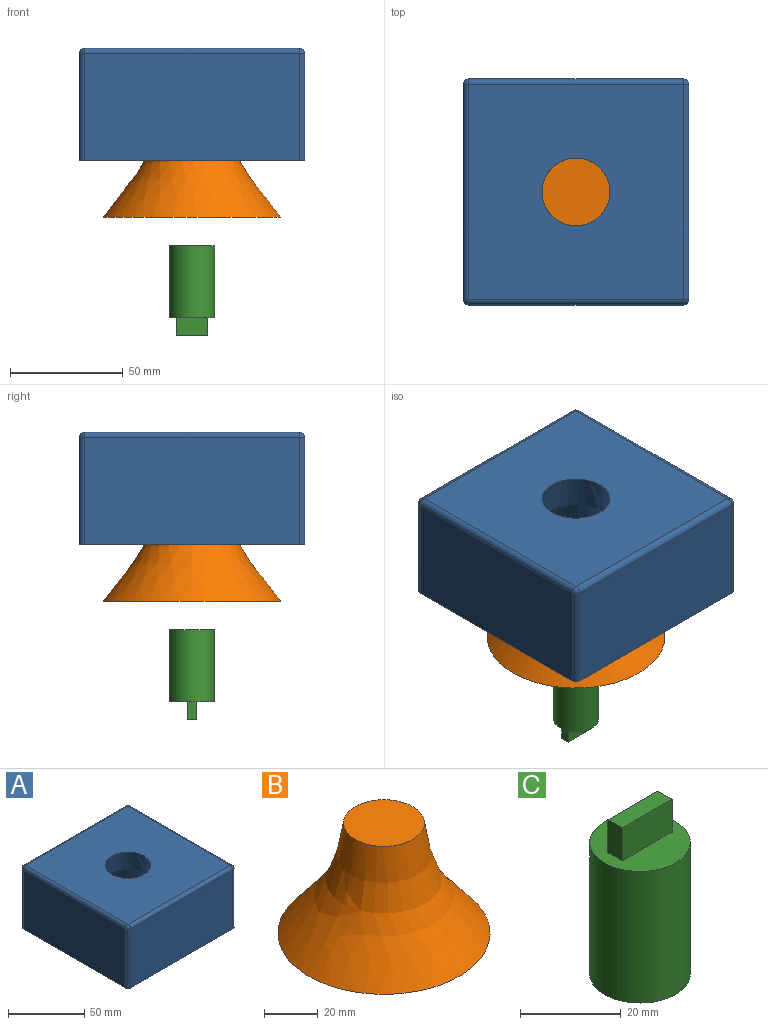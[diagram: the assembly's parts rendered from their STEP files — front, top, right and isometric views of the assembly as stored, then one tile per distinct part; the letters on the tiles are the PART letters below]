
ASSEMBLY  parts=3 mates=2
PART A: 19 faces, bbox 100x100x50 mm
  f0: plane 95x47.5mm, normal (0,-1,0), area 4512.5mm2, adj f5,f9,f15,f18
  f1: plane 95x47.5mm, normal (1,0,0), area 4512.5mm2, adj f5,f12,f16,f18
  f2: plane 95x47.5mm, normal (0,1,0), area 4512.5mm2, adj f5,f7,f11,f12
  f3: plane 95x47.5mm, normal (-1,0,0), area 4512.5mm2, adj f5,f7,f9,f10
  f4: plane 95x95mm, normal (0,0,1), area 8318.1mm2, adj f6,f10,f11,f15,f16
  f5: plane 100x100mm, normal (0,0,-1), area 5132.4mm2, adj f0,f1,f2,f3,f6,f7,f9,f12
  f6: revolved ~78.68x78.68mm, area 8666.1mm2, adj f4,f5
  f7: cylinder r=2.5mm len=47.5mm, axis (0,0,-1), area 186.5mm2, adj f2,f3,f5,f8
  f8: sphere r=2.5mm, area 9.8mm2, adj f7,f10,f11
  f9: cylinder r=2.5mm len=47.5mm, axis (0,0,1), area 186.5mm2, adj f0,f3,f5,f13
  f10: cylinder r=2.5mm len=95mm, axis (0,1,0), area 373.1mm2, adj f3,f4,f8,f13
  f11: cylinder r=2.5mm len=95mm, axis (1,0,0), area 373.1mm2, adj f2,f4,f8,f14
  f12: cylinder r=2.5mm len=47.5mm, axis (0,0,1), area 186.5mm2, adj f1,f2,f5,f14
  f13: sphere r=2.5mm, area 9.8mm2, adj f9,f10,f15
  f14: sphere r=2.5mm, area 9.8mm2, adj f11,f12,f16
  f15: cylinder r=2.5mm len=95mm, axis (-1,0,0), area 373.1mm2, adj f0,f4,f13,f17
  f16: cylinder r=2.5mm len=95mm, axis (0,-1,0), area 373.1mm2, adj f1,f4,f14,f17
  f17: sphere r=2.5mm, area 9.8mm2, adj f15,f16,f18
  f18: cylinder r=2.5mm len=47.5mm, axis (0,0,-1), area 186.5mm2, adj f0,f1,f5,f17
PART B: 5 faces, bbox 78.7x78.7x50 mm
  f0: plane 30x30mm, normal (0,0,1), area 706.9mm2, adj f1
  f1: revolved ~78.68x78.68mm, area 8666.1mm2, adj f0,f2
  f2: plane 78.68x78.68mm, normal (0,0,-1), area 4548mm2, adj f1,f3
  f3: cylinder r=10mm len=40mm, axis (0,0,-1), area 2513.3mm2, adj f2,f4
  f4: plane 20x20mm, normal (0,0,-1), area 314.2mm2, adj f3
PART C: 10 faces, bbox 20x20x40 mm
  f0: cylinder r=10mm len=32mm, axis (0,0,-1), area 2010.6mm2, adj f1,f2
  f1: plane 20x20mm, normal (0,0,1), area 258.2mm2, adj f0,f5,f6,f7,f8
  f2: plane 20x20mm, normal (0,0,-1), area 87.2mm2, adj f0,f3
  f3: cylinder r=8.5mm len=30.5mm, axis (0,0,-1), area 1628.9mm2, adj f2,f4
  f4: plane 17x17mm, normal (0,0,-1), area 227mm2, adj f3
  f5: plane 8x4mm, normal (-1,0,0), area 32mm2, adj f1,f6,f8,f9
  f6: plane 14x8mm, normal (0,-1,0), area 112mm2, adj f1,f5,f7,f9
  f7: plane 8x4mm, normal (1,0,0), area 32mm2, adj f1,f6,f8,f9
  f8: plane 14x8mm, normal (0,1,0), area 112mm2, adj f1,f5,f7,f9
  f9: plane 14x4mm, normal (0,0,1), area 56mm2, adj f5,f6,f7,f8
PLACE A t=(4.96,13.99,-1.33)mm
PLACE B t=(4.96,13.99,-26.24)mm fixed
PLACE C rot(axis=(1,0,0),180deg) t=(4.96,13.99,-38.81)mm
MATE slider B.f3 <-> A.f6  axis (0,0,-1) through (4.96,13.99,-2.93)mm
MATE slider B.f3 <-> C.f0  axis (0,0,-1) through (4.96,13.99,13.76)mm
